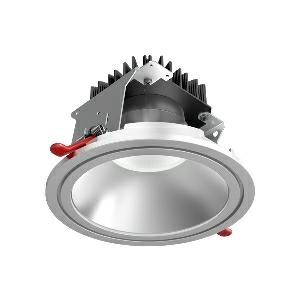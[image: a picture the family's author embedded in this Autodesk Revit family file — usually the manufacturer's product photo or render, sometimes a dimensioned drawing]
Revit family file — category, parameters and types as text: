
# Revit family: dotoo_spot_-_dse_1000_830_00806084_7ffe
name_source: partatom
category: Lighting Fixtures
units: mm (PartAtom-declared; Revit-internal decimal feet)

## family parameters
Cut with Voids When Loaded = No
Host = Face
Light Source = No
Part Type = Normal
Room Calculation Point = No
Round Connector Dimension = Use Diameter
Shared = No

## types (1)
- DOTOO.spot - DSE 1000/830 (1 x LED, 1400 lm, 3000K)
    Apparent Load = 14 VA
    Approval mark = CE
    CIE Flux Codes = 87 99 100 100 100
    Color Rendering = 80-89
    Color Temperature = 3000K
    Control Gear = Electronic ballast
    Default Elevation = 1800 mm
    Description = DSE 1000/830|Recessed luminaire|light source: LED|work equipment: Electronic ballast|connected load: 220-240 V, 50/60 Hz|Power consumption: approx. 14 W|standby: approx. 0,20|power factor: approx. 0,900|luminous flux: 1400 lm|luminous efficacy: 100 lm/W|light distribution: Direct|direct ratio: approx. 100 %|colour temperature: Warm white, ca. 3000 K|color rendering index (CRI): >= 80|chromaticity tolerance:  3 SDCM|System of protection: IP 20|class of protection: II|technology: Switchable|operation: External|luminaire body|material: Sheet metal|colour: White|weight (net): approx. 0.7 kg|mains lead: 0.35 m Connector|Fastening: Tension spring|glare control: Prism aperture|luminance(L65): <= 2100 cd/m|unified glare rating(4H 8H): <=  19|special features: Flicker-free, Low installation depth thanks to external ballast, Suitable as emergency lighting, Ceiling installation without tools by means of tension springs, Strain relief with the possibility of through-wiring, As supplement for room depths and walking areas|
    Height = 0 mm  [stored 0 ft]
    Lamp = 1 x LED
    Lamp Light Flux = 1400 lm
    Lamp count = 1
    Length = 166 mm
    Luminous efficacy = 100 lm/W
    Manufacturer = Waldmann
    ModVariant = No
    Model = 00806084
    Mounting Place = Ceiling
    Mounting Type = Recessed
    Number of Poles = 1
    OnlyDefault = Yes
    Power Factor = 1
    Product Name = DOTOO.spot - DSE 1000/830
    Product group = Recessed luminaire
    ProductGroupID = 4
    Protection Class = Protection class II
    Protection Degree = IP 20
    RLX_Detail_Level = 1
    RLX_Emergency_Light_Flux = 0 lm
    RLX_Emergency_Type = 0
    RLX_Emergency_Type_DB = No
    RlxData = <blob elided: 54005 chars, md5=18b898cf>
    Socket = socket
    Standby Power = 0 W
    System Light Flux = 1400 lm
    System Power = 14 W
    Type Comments = Product without accessories
    Type Image = 114272000-00806084.jpg
    URL = http://relux.com
    VarID = ---
    Voltage = 230 V
    Voltage Range = 220-240 V
    Weight = 0.00 kg
    Width = 0 mm  [stored 0 ft]

note: [stored X ft] marks values corroborated as IEEE doubles in the binary element streams (Revit-internal decimal feet)

## geometry (parser evidence)
native form markers: Blend x4, Sweep x10
no freeform markers — native parametric forms only
